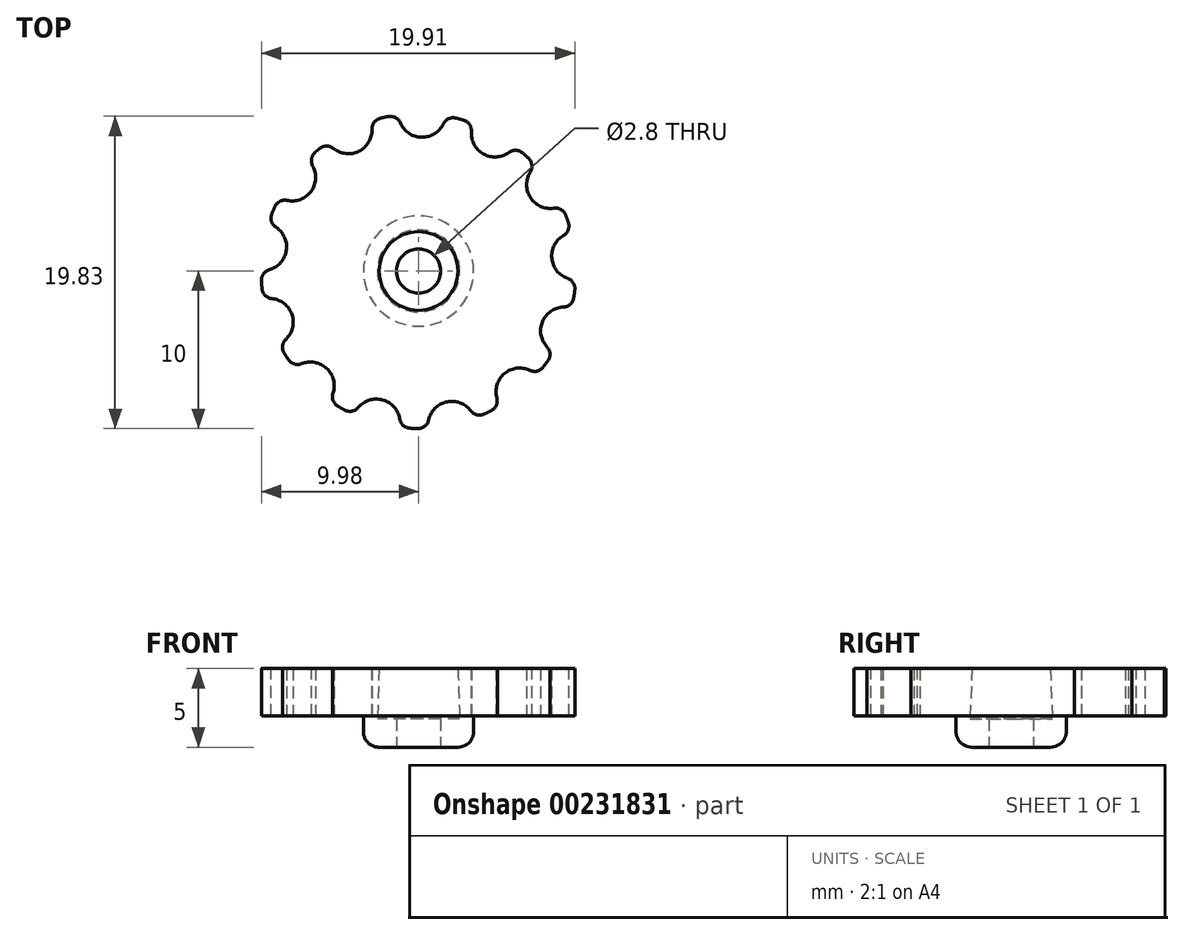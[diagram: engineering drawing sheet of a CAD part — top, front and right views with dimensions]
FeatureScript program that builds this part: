
annotation { "Feature Type Name" : "Feature", "Feature Type Description" : "" }
export const myFeature = defineFeature(function(context is Context, id is Id, definition is map)
    precondition{}
    {
        {
            var Q0;
            Q0=qCreatedBy(makeId("Top.planeOp"),FACE);
            var sketch = newSketch(context, id + "F0", { "sketchPlane" : qUnion([Q0])});
            skCircle(sketch, "E0", {"center": v(0, 0) * mm, "radius": 10 * mm});
            skArc(sketch, "E1", {"start": v(-5.75, 8.18) * mm, "mid": v(-3.79, 7.6) * mm, "end": v(-3.07, 9.52) * mm});
            skArc(sketch, "E2.1.0", {"start": v(-1.27, 9.92) * mm, "mid": v(0.2, 8.5) * mm, "end": v(1.72, 9.85) * mm});
            skArc(sketch, "E2.2.0", {"start": v(3.5, 9.37) * mm, "mid": v(4.13, 7.43) * mm, "end": v(6.1, 7.92) * mm});
            skArc(sketch, "E2.3.0", {"start": v(7.45, 6.67) * mm, "mid": v(7.11, 4.66) * mm, "end": v(9.1, 4.16) * mm});
            skArc(sketch, "E2.4.0", {"start": v(9.7, 2.43) * mm, "mid": v(8.46, 0.8) * mm, "end": v(9.99, -0.55) * mm});
            skArc(sketch, "E2.5.0", {"start": v(9.72, -2.37) * mm, "mid": v(7.87, -3.22) * mm, "end": v(8.58, -5.13) * mm});
            skArc(sketch, "E2.6.0", {"start": v(7.5, -6.62) * mm, "mid": v(5.46, -6.51) * mm, "end": v(5.2, -8.54) * mm});
            skArc(sketch, "E2.7.0", {"start": v(3.55, -9.35) * mm, "mid": v(1.8, -8.3) * mm, "end": v(0.63, -9.98) * mm});
            skArc(sketch, "E2.8.0", {"start": v(-1.2, -9.93) * mm, "mid": v(-2.28, -8.19) * mm, "end": v(-4.09, -9.13) * mm});
            skArc(sketch, "E2.9.0", {"start": v(-5.7, -8.22) * mm, "mid": v(-5.83, -6.19) * mm, "end": v(-7.87, -6.17) * mm});
            skArc(sketch, "E2.10.0", {"start": v(-8.86, -4.63) * mm, "mid": v(-8.04, -2.76) * mm, "end": v(-9.84, -1.8) * mm});
            skArc(sketch, "E2.11.0", {"start": v(-10, 0.03) * mm, "mid": v(-8.4, 1.3) * mm, "end": v(-9.54, 2.99) * mm});
            skLineSegment(sketch, "E2.anchor1", {"start": v(0, 0) * mm, "end": v(-4.46, 8.95) * mm, "construction": true});
            skLineSegment(sketch, "E2.anchor2", {"start": v(0, 0) * mm, "end": v(-8.03, 5.95) * mm, "construction": true});
            skArc(sketch, "E3.1.12.0", {"start": v(-8.83, 4.68) * mm, "mid": v(-6.83, 5.06) * mm, "end": v(-7.05, 7.09) * mm});
            skCircle(sketch, "E4", {"center": v(0, 0) * mm, "radius": 1.4 * mm});
            skSolve(sketch);
        }
        {
            var Q0;
            {var subQ9=sQuery(id+"F0.wireOp",EDGE,"E1");Q0=makeQuery(id+"F0.imprint","IMPRINT",FACE,{"disambiguationData":[TD([[makeQuery(id+"F0.imprint","IMPRINT",EDGE,{"derivedFrom":subQ9}),-1.0]])]});}
            extrude(context, id + "F1", {"entities" : qUnion([Q0]), "depth" : 3 * mm});
        }
        {
            var Q0;
            Q0=makeQuery(id+"F1.opExtrude","CAP_FACE",FACE,{"disambiguationData":[OSD([sQuery(id+"F0.wireOp",EDGE,"E0"),sQuery(id+"F0.wireOp",EDGE,"E1"),sQuery(id+"F0.wireOp",EDGE,"E2.1.0"),sQuery(id+"F0.wireOp",EDGE,"E2.2.0"),sQuery(id+"F0.wireOp",EDGE,"E2.3.0"),sQuery(id+"F0.wireOp",EDGE,"E2.4.0"),sQuery(id+"F0.wireOp",EDGE,"E2.5.0"),sQuery(id+"F0.wireOp",EDGE,"E2.6.0"),sQuery(id+"F0.wireOp",EDGE,"E2.7.0"),sQuery(id+"F0.wireOp",EDGE,"E2.8.0"),sQuery(id+"F0.wireOp",EDGE,"E2.9.0"),sQuery(id+"F0.wireOp",EDGE,"E2.10.0"),sQuery(id+"F0.wireOp",EDGE,"E2.11.0"),sQuery(id+"F0.wireOp",EDGE,"E3.1.12.0")])],"isStart":true});
            var sketch = newSketch(context, id + "F2", { "sketchPlane" : qUnion([Q0])});
            skSolve(sketch);
        }
        {
            var Q0;
            {var subQ5=sQuery(id+"F0.wireOp",EDGE,"E1");Q0=makeQuery(id+"F2.imprint","IMPRINT",FACE,{"disambiguationData":[TD([[makeQuery(id+"F2.imprint","IMPRINT",EDGE,{"derivedFrom":makeQuery(id+"F1.opExtrude","CAP_EDGE",EDGE,{"disambiguationData":[OSD([subQ5])],"isStart":true})}),1.0]])]});}
            var sketch = newSketch(context, id + "F3", { "sketchPlane" : qUnion([Q0])});
            skCircle(sketch, "E5", {"center": v(0, 0) * mm, "radius": 3.5 * mm});
            skSolve(sketch);
        }
        {
            var Q0;
            Q0=makeQuery(id+"F3.imprint","IMPRINT",FACE,{"disambiguationData":[TD([[makeQuery(id+"F3.imprint","IMPRINT",EDGE,{"derivedFrom":sQuery(id+"F3.wireOp",EDGE,"E5")}),1.0]])]});
            extrude(context, id + "F4", {"entities" : qUnion([Q0]), "operationType" : NewBodyOperationType.ADD, "depth" : 2 * mm});
        }
        {
            var Q0;
            Q0=makeQuery(id+"F1.opExtrude","CAP_FACE",FACE,{"disambiguationData":[OSD([sQuery(id+"F0.wireOp",EDGE,"E0"),sQuery(id+"F0.wireOp",EDGE,"E1"),sQuery(id+"F0.wireOp",EDGE,"E2.1.0"),sQuery(id+"F0.wireOp",EDGE,"E2.2.0"),sQuery(id+"F0.wireOp",EDGE,"E2.3.0"),sQuery(id+"F0.wireOp",EDGE,"E2.4.0"),sQuery(id+"F0.wireOp",EDGE,"E2.5.0"),sQuery(id+"F0.wireOp",EDGE,"E2.6.0"),sQuery(id+"F0.wireOp",EDGE,"E2.7.0"),sQuery(id+"F0.wireOp",EDGE,"E2.8.0"),sQuery(id+"F0.wireOp",EDGE,"E2.9.0"),sQuery(id+"F0.wireOp",EDGE,"E2.10.0"),sQuery(id+"F0.wireOp",EDGE,"E2.11.0"),sQuery(id+"F0.wireOp",EDGE,"E3.1.12.0"),sQuery(id+"F0.wireOp",EDGE,"E4")])],"isStart":false});
            var sketch = newSketch(context, id + "F5", { "sketchPlane" : qUnion([Q0])});
            skCircle(sketch, "E6", {"center": v(0, 0) * mm, "radius": 2.5 * mm});
            skSolve(sketch);
        }
        {
            var Q0;
            Q0 = qSketchRegion(id + "F5", true);
            extrude(context, id + "F6", {"entities" : qUnion([Q0]), "operationType" : NewBodyOperationType.REMOVE, "oppositeDirection" : true, "depth" : 3.2 * mm, "hasDraft" : true, "draftAngle" : 2 * degree});
        }
        {
            var Q0;
            {var subQ0=sQuery(id+"F0.wireOp",EDGE,"E2.10.0");var subQ1=sQuery(id+"F0.wireOp",EDGE,"E0");Q0=makeQuery(id+"F1.opExtrude","SWEPT_EDGE",EDGE,{"disambiguationData":[OSD([subQ1,subQ0]),TDD([makeQuery(id+"F0.imprint","INTERSECT",VERTEX,{"disambiguationData":[OD(1.0)],"derivedFrom":[subQ1,subQ0]})])]});}
            var Q1;
            {var subQ0=sQuery(id+"F0.wireOp",EDGE,"E2.9.0");var subQ1=sQuery(id+"F0.wireOp",EDGE,"E0");Q1=makeQuery(id+"F1.opExtrude","SWEPT_EDGE",EDGE,{"disambiguationData":[OSD([subQ1,subQ0]),TDD([makeQuery(id+"F0.imprint","INTERSECT",VERTEX,{"disambiguationData":[OD(1.0)],"derivedFrom":[subQ1,subQ0]})])]});}
            var Q2;
            {var subQ0=sQuery(id+"F0.wireOp",EDGE,"E2.8.0");var subQ1=sQuery(id+"F0.wireOp",EDGE,"E0");Q2=makeQuery(id+"F1.opExtrude","SWEPT_EDGE",EDGE,{"disambiguationData":[OSD([subQ1,subQ0]),TDD([makeQuery(id+"F0.imprint","INTERSECT",VERTEX,{"disambiguationData":[OD(1.0)],"derivedFrom":[subQ1,subQ0]})])]});}
            var Q3;
            {var subQ0=sQuery(id+"F0.wireOp",EDGE,"E2.7.0");var subQ1=sQuery(id+"F0.wireOp",EDGE,"E0");Q3=makeQuery(id+"F1.opExtrude","SWEPT_EDGE",EDGE,{"disambiguationData":[OSD([subQ1,subQ0]),TDD([makeQuery(id+"F0.imprint","INTERSECT",VERTEX,{"disambiguationData":[OD(1.0)],"derivedFrom":[subQ1,subQ0]})])]});}
            var Q4;
            {var subQ0=sQuery(id+"F0.wireOp",EDGE,"E2.8.0");var subQ1=sQuery(id+"F0.wireOp",EDGE,"E0");Q4=makeQuery(id+"F1.opExtrude","SWEPT_EDGE",EDGE,{"disambiguationData":[OSD([subQ1,subQ0]),TDD([makeQuery(id+"F0.imprint","INTERSECT",VERTEX,{"disambiguationData":[OD(0.0)],"derivedFrom":[subQ1,subQ0]})])]});}
            var Q5;
            {var subQ0=sQuery(id+"F0.wireOp",EDGE,"E2.9.0");var subQ1=sQuery(id+"F0.wireOp",EDGE,"E0");Q5=makeQuery(id+"F1.opExtrude","SWEPT_EDGE",EDGE,{"disambiguationData":[OSD([subQ1,subQ0]),TDD([makeQuery(id+"F0.imprint","INTERSECT",VERTEX,{"disambiguationData":[OD(0.0)],"derivedFrom":[subQ1,subQ0]})])]});}
            var Q6;
            {var subQ0=sQuery(id+"F0.wireOp",EDGE,"E2.10.0");var subQ1=sQuery(id+"F0.wireOp",EDGE,"E0");Q6=makeQuery(id+"F1.opExtrude","SWEPT_EDGE",EDGE,{"disambiguationData":[OSD([subQ1,subQ0]),TDD([makeQuery(id+"F0.imprint","INTERSECT",VERTEX,{"disambiguationData":[OD(0.0)],"derivedFrom":[subQ1,subQ0]})])]});}
            var Q7;
            {var subQ0=sQuery(id+"F0.wireOp",EDGE,"E2.11.0");var subQ1=sQuery(id+"F0.wireOp",EDGE,"E0");Q7=makeQuery(id+"F1.opExtrude","SWEPT_EDGE",EDGE,{"disambiguationData":[OSD([subQ1,subQ0]),TDD([makeQuery(id+"F0.imprint","INTERSECT",VERTEX,{"disambiguationData":[OD(0.0)],"derivedFrom":[subQ1,subQ0]})])]});}
            var Q8;
            {var subQ0=sQuery(id+"F0.wireOp",EDGE,"E3.1.12.0");var subQ1=sQuery(id+"F0.wireOp",EDGE,"E0");Q8=makeQuery(id+"F1.opExtrude","SWEPT_EDGE",EDGE,{"disambiguationData":[OSD([subQ1,subQ0]),TDD([makeQuery(id+"F0.imprint","INTERSECT",VERTEX,{"disambiguationData":[OD(0.0)],"derivedFrom":[subQ1,subQ0]})])]});}
            var Q9;
            {var subQ0=sQuery(id+"F0.wireOp",EDGE,"E2.11.0");var subQ1=sQuery(id+"F0.wireOp",EDGE,"E0");Q9=makeQuery(id+"F1.opExtrude","SWEPT_EDGE",EDGE,{"disambiguationData":[OSD([subQ1,subQ0]),TDD([makeQuery(id+"F0.imprint","INTERSECT",VERTEX,{"disambiguationData":[OD(1.0)],"derivedFrom":[subQ1,subQ0]})])]});}
            var Q10;
            {var subQ0=sQuery(id+"F0.wireOp",EDGE,"E1");var subQ1=sQuery(id+"F0.wireOp",EDGE,"E0");Q10=makeQuery(id+"F1.opExtrude","SWEPT_EDGE",EDGE,{"disambiguationData":[OSD([subQ1,subQ0]),TDD([makeQuery(id+"F0.imprint","INTERSECT",VERTEX,{"disambiguationData":[OD(0.0)],"derivedFrom":[subQ1,subQ0]})])]});}
            var Q11;
            {var subQ0=sQuery(id+"F0.wireOp",EDGE,"E3.1.12.0");var subQ1=sQuery(id+"F0.wireOp",EDGE,"E0");Q11=makeQuery(id+"F1.opExtrude","SWEPT_EDGE",EDGE,{"disambiguationData":[OSD([subQ1,subQ0]),TDD([makeQuery(id+"F0.imprint","INTERSECT",VERTEX,{"disambiguationData":[OD(1.0)],"derivedFrom":[subQ1,subQ0]})])]});}
            var Q12;
            {var subQ0=sQuery(id+"F0.wireOp",EDGE,"E1");var subQ1=sQuery(id+"F0.wireOp",EDGE,"E0");Q12=makeQuery(id+"F1.opExtrude","SWEPT_EDGE",EDGE,{"disambiguationData":[OSD([subQ1,subQ0]),TDD([makeQuery(id+"F0.imprint","INTERSECT",VERTEX,{"disambiguationData":[OD(1.0)],"derivedFrom":[subQ1,subQ0]})])]});}
            var Q13;
            {var subQ0=sQuery(id+"F0.wireOp",EDGE,"E2.1.0");var subQ1=sQuery(id+"F0.wireOp",EDGE,"E0");Q13=makeQuery(id+"F1.opExtrude","SWEPT_EDGE",EDGE,{"disambiguationData":[OSD([subQ1,subQ0]),TDD([makeQuery(id+"F0.imprint","INTERSECT",VERTEX,{"disambiguationData":[OD(0.0)],"derivedFrom":[subQ1,subQ0]})])]});}
            var Q14;
            {var subQ0=sQuery(id+"F0.wireOp",EDGE,"E2.1.0");var subQ1=sQuery(id+"F0.wireOp",EDGE,"E0");Q14=makeQuery(id+"F1.opExtrude","SWEPT_EDGE",EDGE,{"disambiguationData":[OSD([subQ1,subQ0]),TDD([makeQuery(id+"F0.imprint","INTERSECT",VERTEX,{"disambiguationData":[OD(1.0)],"derivedFrom":[subQ1,subQ0]})])]});}
            var Q15;
            {var subQ0=sQuery(id+"F0.wireOp",EDGE,"E2.2.0");var subQ1=sQuery(id+"F0.wireOp",EDGE,"E0");Q15=makeQuery(id+"F1.opExtrude","SWEPT_EDGE",EDGE,{"disambiguationData":[OSD([subQ1,subQ0]),TDD([makeQuery(id+"F0.imprint","INTERSECT",VERTEX,{"disambiguationData":[OD(0.0)],"derivedFrom":[subQ1,subQ0]})])]});}
            var Q16;
            {var subQ0=sQuery(id+"F0.wireOp",EDGE,"E2.2.0");var subQ1=sQuery(id+"F0.wireOp",EDGE,"E0");Q16=makeQuery(id+"F1.opExtrude","SWEPT_EDGE",EDGE,{"disambiguationData":[OSD([subQ1,subQ0]),TDD([makeQuery(id+"F0.imprint","INTERSECT",VERTEX,{"disambiguationData":[OD(1.0)],"derivedFrom":[subQ1,subQ0]})])]});}
            var Q17;
            {var subQ0=sQuery(id+"F0.wireOp",EDGE,"E2.3.0");var subQ1=sQuery(id+"F0.wireOp",EDGE,"E0");Q17=makeQuery(id+"F1.opExtrude","SWEPT_EDGE",EDGE,{"disambiguationData":[OSD([subQ1,subQ0]),TDD([makeQuery(id+"F0.imprint","INTERSECT",VERTEX,{"disambiguationData":[OD(1.0)],"derivedFrom":[subQ1,subQ0]})])]});}
            var Q18;
            {var subQ0=sQuery(id+"F0.wireOp",EDGE,"E2.3.0");var subQ1=sQuery(id+"F0.wireOp",EDGE,"E0");Q18=makeQuery(id+"F1.opExtrude","SWEPT_EDGE",EDGE,{"disambiguationData":[OSD([subQ1,subQ0]),TDD([makeQuery(id+"F0.imprint","INTERSECT",VERTEX,{"disambiguationData":[OD(0.0)],"derivedFrom":[subQ1,subQ0]})])]});}
            var Q19;
            {var subQ0=sQuery(id+"F0.wireOp",EDGE,"E2.4.0");var subQ1=sQuery(id+"F0.wireOp",EDGE,"E0");Q19=makeQuery(id+"F1.opExtrude","SWEPT_EDGE",EDGE,{"disambiguationData":[OSD([subQ1,subQ0]),TDD([makeQuery(id+"F0.imprint","INTERSECT",VERTEX,{"disambiguationData":[OD(0.0)],"derivedFrom":[subQ1,subQ0]})])]});}
            var Q20;
            {var subQ0=sQuery(id+"F0.wireOp",EDGE,"E2.4.0");var subQ1=sQuery(id+"F0.wireOp",EDGE,"E0");Q20=makeQuery(id+"F1.opExtrude","SWEPT_EDGE",EDGE,{"disambiguationData":[OSD([subQ1,subQ0]),TDD([makeQuery(id+"F0.imprint","INTERSECT",VERTEX,{"disambiguationData":[OD(1.0)],"derivedFrom":[subQ1,subQ0]})])]});}
            var Q21;
            {var subQ0=sQuery(id+"F0.wireOp",EDGE,"E2.5.0");var subQ1=sQuery(id+"F0.wireOp",EDGE,"E0");Q21=makeQuery(id+"F1.opExtrude","SWEPT_EDGE",EDGE,{"disambiguationData":[OSD([subQ1,subQ0]),TDD([makeQuery(id+"F0.imprint","INTERSECT",VERTEX,{"disambiguationData":[OD(0.0)],"derivedFrom":[subQ1,subQ0]})])]});}
            var Q22;
            {var subQ0=sQuery(id+"F0.wireOp",EDGE,"E2.5.0");var subQ1=sQuery(id+"F0.wireOp",EDGE,"E0");Q22=makeQuery(id+"F1.opExtrude","SWEPT_EDGE",EDGE,{"disambiguationData":[OSD([subQ1,subQ0]),TDD([makeQuery(id+"F0.imprint","INTERSECT",VERTEX,{"disambiguationData":[OD(1.0)],"derivedFrom":[subQ1,subQ0]})])]});}
            var Q23;
            {var subQ0=sQuery(id+"F0.wireOp",EDGE,"E2.6.0");var subQ1=sQuery(id+"F0.wireOp",EDGE,"E0");Q23=makeQuery(id+"F1.opExtrude","SWEPT_EDGE",EDGE,{"disambiguationData":[OSD([subQ1,subQ0]),TDD([makeQuery(id+"F0.imprint","INTERSECT",VERTEX,{"disambiguationData":[OD(0.0)],"derivedFrom":[subQ1,subQ0]})])]});}
            var Q24;
            {var subQ0=sQuery(id+"F0.wireOp",EDGE,"E2.6.0");var subQ1=sQuery(id+"F0.wireOp",EDGE,"E0");Q24=makeQuery(id+"F1.opExtrude","SWEPT_EDGE",EDGE,{"disambiguationData":[OSD([subQ1,subQ0]),TDD([makeQuery(id+"F0.imprint","INTERSECT",VERTEX,{"disambiguationData":[OD(1.0)],"derivedFrom":[subQ1,subQ0]})])]});}
            var Q25;
            {var subQ0=sQuery(id+"F0.wireOp",EDGE,"E2.7.0");var subQ1=sQuery(id+"F0.wireOp",EDGE,"E0");Q25=makeQuery(id+"F1.opExtrude","SWEPT_EDGE",EDGE,{"disambiguationData":[OSD([subQ1,subQ0]),TDD([makeQuery(id+"F0.imprint","INTERSECT",VERTEX,{"disambiguationData":[OD(0.0)],"derivedFrom":[subQ1,subQ0]})])]});}
            fillet(context, id + "F7", {"entities" : qUnion([Q0, Q1, Q2, Q3, Q4, Q5, Q6, Q7, Q8, Q9, Q10, Q11, Q12, Q13, Q14, Q15, Q16, Q17, Q18, Q19, Q20, Q21, Q22, Q23, Q24, Q25]), "radius" : .7 * mm, "tangentPropagation" : true, "allowEdgeOverflow" : false});
        }
        {
            var Q0;
            Q0=makeQuery(id+"F4.opExtrude","CAP_EDGE",EDGE,{"disambiguationData":[OSD([sQuery(id+"F3.wireOp",EDGE,"E5")])],"isStart":true});
            var Q1;
            Q1=makeQuery(id+"F4.opExtrude","CAP_EDGE",EDGE,{"disambiguationData":[OSD([sQuery(id+"F3.wireOp",EDGE,"E5")])],"isStart":false});
            fillet(context, id + "F8", {"entities" : qUnion([Q0, Q1]), "radius" : 1 * mm, "tangentPropagation" : true, "allowEdgeOverflow" : false});
        }
    });
